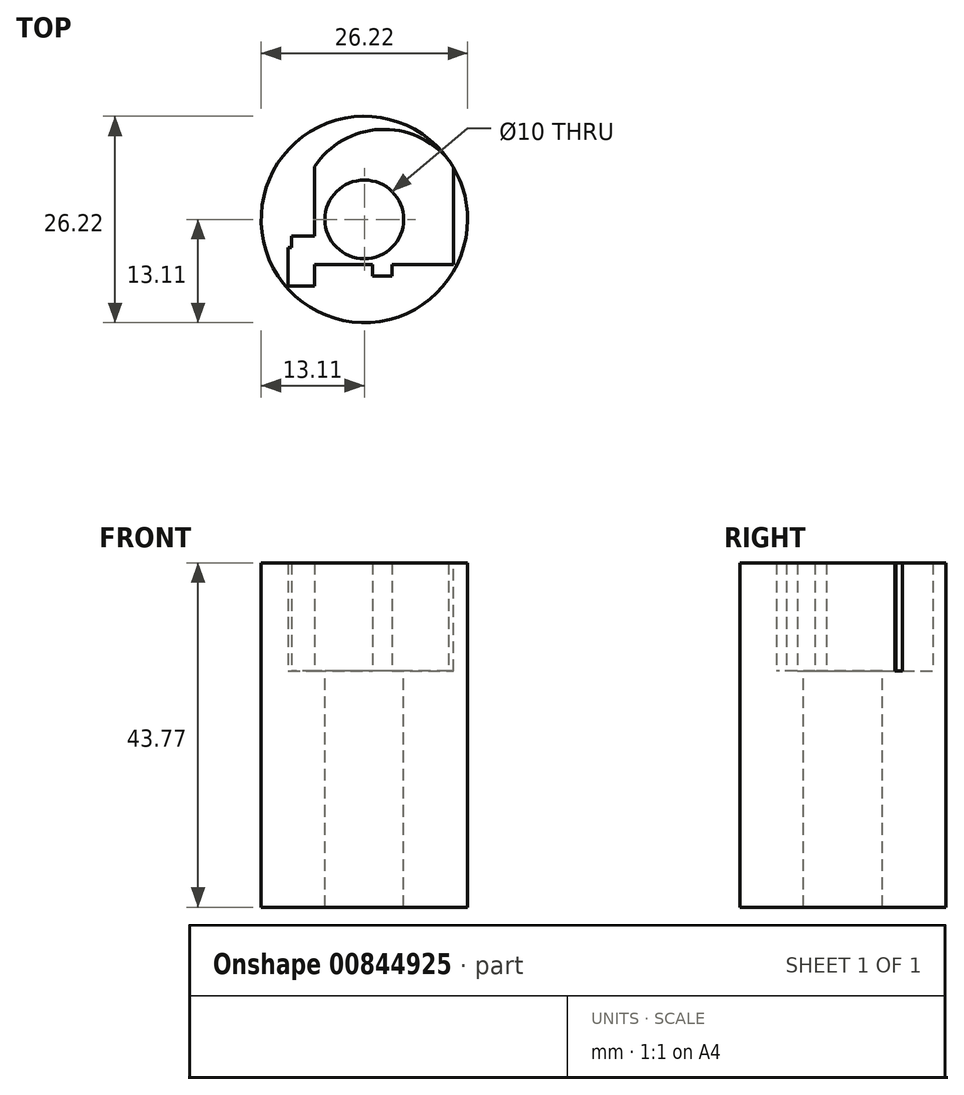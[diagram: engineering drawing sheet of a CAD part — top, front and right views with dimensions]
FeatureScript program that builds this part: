
annotation { "Feature Type Name" : "Feature", "Feature Type Description" : "" }
export const myFeature = defineFeature(function(context is Context, id is Id, definition is map)
    precondition{}
    {
        {
            var Q0;
            Q0=qCreatedBy(makeId("Top.planeOp"),FACE);
            var sketch = newSketch(context, id + "F0", { "sketchPlane" : qUnion([Q0])});
            skCircle(sketch, "E0", {"center": v(0, 0) * mm, "radius": 13.12 * mm, "construction": true});
            skSolve(sketch);
        }
        {
            var Q0;
            Q0=qCreatedBy(makeId("Top.planeOp"),FACE);
            var sketch = newSketch(context, id + "F1", { "sketchPlane" : qUnion([Q0])});
            skCircle(sketch, "E1", {"center": v(0, 0) * mm, "radius": 13.1 * mm});
            skCircle(sketch, "E2", {"center": v(0, 0) * mm, "radius": 5 * mm});
            skCircle(sketch, "E3.0", {"center": v(0, 0) * mm, "radius": 13.12 * mm});
            skSolve(sketch);
        }
        {
            var Q0;
            Q0=makeQuery(id+"F1.imprint","IMPRINT",FACE,{"disambiguationData":[TD([[makeQuery(id+"F1.imprint","IMPRINT",EDGE,{"derivedFrom":sQuery(id+"F1.wireOp",EDGE,"E1")}),1.0]])]});
            extrude(context, id + "F2", {"entities" : qUnion([Q0]), "oppositeDirection" : true, "depth" : 15 * mm, "offsetDistance" : 25 * mm, "hasSecondDirection" : true, "secondDirectionOppositeDirection" : false, "secondDirectionDepth" : 28.77 * mm});
        }
        {
            var Q0;
            Q0=qCreatedBy(makeId("Top.planeOp"),FACE);
            cPlane(context, id + "F3", {"entities" : qUnion([Q0]), "cplaneType" : CPlaneType.OFFSET, "offset" : 15 * mm, "width" : 150 * mm, "height" : 150 * mm});
        }
        {
            var Q0;
            Q0=qCreatedBy(id+"F3.planeOp",FACE);
            var sketch = newSketch(context, id + "F4", { "sketchPlane" : qUnion([Q0])});
            skLineSegment(sketch, "E4.bottom", {"start": v(-9.28, -3.55) * mm, "end": v(11.32, -3.55) * mm});
            skLineSegment(sketch, "E4.top", {"start": v(-6.34, -5.76) * mm, "end": v(11.32, -5.76) * mm});
            skLineSegment(sketch, "E4.right", {"start": v(11.32, -3.55) * mm, "end": v(11.32, -5.76) * mm});
            skLineSegment(sketch, "E5.0", {"start": v(-6.34, -5.76) * mm, "end": v(1.01, -5.76) * mm});
            skLineSegment(sketch, "E6.top", {"start": v(3.52, -7.17) * mm, "end": v(1.01, -7.17) * mm});
            skLineSegment(sketch, "E6.left", {"start": v(3.52, -5.76) * mm, "end": v(3.52, -7.17) * mm});
            skLineSegment(sketch, "E6.right", {"start": v(1.01, -5.76) * mm, "end": v(1.01, -7.17) * mm});
            skLineSegment(sketch, "E7.0", {"start": v(10.91, -3.55) * mm, "end": v(10.91, -5.76) * mm});
            skLineSegment(sketch, "E8.0", {"start": v(-9.69, -3.55) * mm, "end": v(-9.69, -5.76) * mm});
            skLineSegment(sketch, "E9.top", {"start": v(-9.69, -8.47) * mm, "end": v(-6.34, -8.47) * mm});
            skLineSegment(sketch, "E9.left", {"start": v(-9.69, -5.76) * mm, "end": v(-9.69, -8.47) * mm});
            skLineSegment(sketch, "E9.right", {"start": v(-6.34, -5.76) * mm, "end": v(-6.34, -8.47) * mm});
            skLineSegment(sketch, "E10.trimOffspring", {"start": v(3.52, -5.76) * mm, "end": v(10.91, -5.76) * mm});
            skLineSegment(sketch, "E11.bottom", {"start": v(-6.34, -3.55) * mm, "end": v(-9.28, -3.55) * mm});
            skLineSegment(sketch, "E11.top", {"start": v(-6.34, -2.11) * mm, "end": v(-9.28, -2.11) * mm});
            skLineSegment(sketch, "E11.left", {"start": v(-6.34, -3.55) * mm, "end": v(-6.34, -2.11) * mm});
            skLineSegment(sketch, "E11.right", {"start": v(-9.28, -3.55) * mm, "end": v(-9.28, -2.11) * mm});
            skLineSegment(sketch, "E12.bottom", {"start": v(11.32, -3.55) * mm, "end": v(-6.34, -3.55) * mm});
            skLineSegment(sketch, "E12.top", {"start": v(11.32, 6.73) * mm, "end": v(-6.34, 6.73) * mm});
            skLineSegment(sketch, "E12.left", {"start": v(11.32, -3.55) * mm, "end": v(11.32, 6.73) * mm});
            skLineSegment(sketch, "E12.right", {"start": v(-6.34, -3.55) * mm, "end": v(-6.34, 6.73) * mm});
            skArc(sketch, "E13", {"start": v(11.32, 6.73) * mm, "mid": v(2.5, 11.44) * mm, "end": v(-6.34, 6.73) * mm});
            skLineSegment(sketch, "E14", {"start": v(-9.69, -3.55) * mm, "end": v(-9.28, -3.55) * mm});
            skSolve(sketch);
        }
        {
            var Q0;
            {var subQ1=sQuery(id+"F4.wireOp",EDGE,"E4.right");var subQ3=sQuery(id+"F4.wireOp",EDGE,"E7.0");var subQ8=makeQuery(id+"F4.imprint","IMPRINT",EDGE,{"derivedFrom":subQ3});var subQ9=sQuery(id+"F4.wireOp",EDGE,"E11.left");var subQ14=makeQuery(id+"F4.imprint","IMPRINT",EDGE,{"derivedFrom":subQ9});var subQ15=makeQuery(id+"F4.imprint","IMPRINT",EDGE,{"derivedFrom":sQuery(id+"F4.wireOp",EDGE,"E12.top")});Q0=qUnion([makeQuery(id+"F4.imprint","IMPRINT",FACE,{"disambiguationData":[TD([[makeQuery(id+"F4.imprint","IMPRINT",EDGE,{"derivedFrom":sQuery(id+"F4.wireOp",EDGE,"E6.top")}),-1.0]])]}),makeQuery(id+"F4.imprint","IMPRINT",FACE,{"disambiguationData":[TD([[subQ8,-1.0]])]}),makeQuery(id+"F4.imprint","IMPRINT",FACE,{"disambiguationData":[TD([[subQ15,-1.0]])]}),makeQuery(id+"F4.imprint","IMPRINT",FACE,{"disambiguationData":[TD([[subQ14,-1.0]])]}),makeQuery(id+"F4.imprint","IMPRINT",FACE,{"disambiguationData":[TD([[makeQuery(id+"F4.imprint","IMPRINT",EDGE,{"derivedFrom":sQuery(id+"F4.wireOp",EDGE,"E11.top")}),1.0]])]}),makeQuery(id+"F4.imprint","IMPRINT",FACE,{"disambiguationData":[TD([[makeQuery(id+"F4.imprint","IMPRINT",EDGE,{"derivedFrom":subQ1}),-1.0]])]})]);}
            extrude(context, id + "F5", {"entities" : qUnion([Q0]), "operationType" : NewBodyOperationType.REMOVE, "depth" : 28.77 * mm, "offsetDistance" : 25 * mm});
        }
    });
